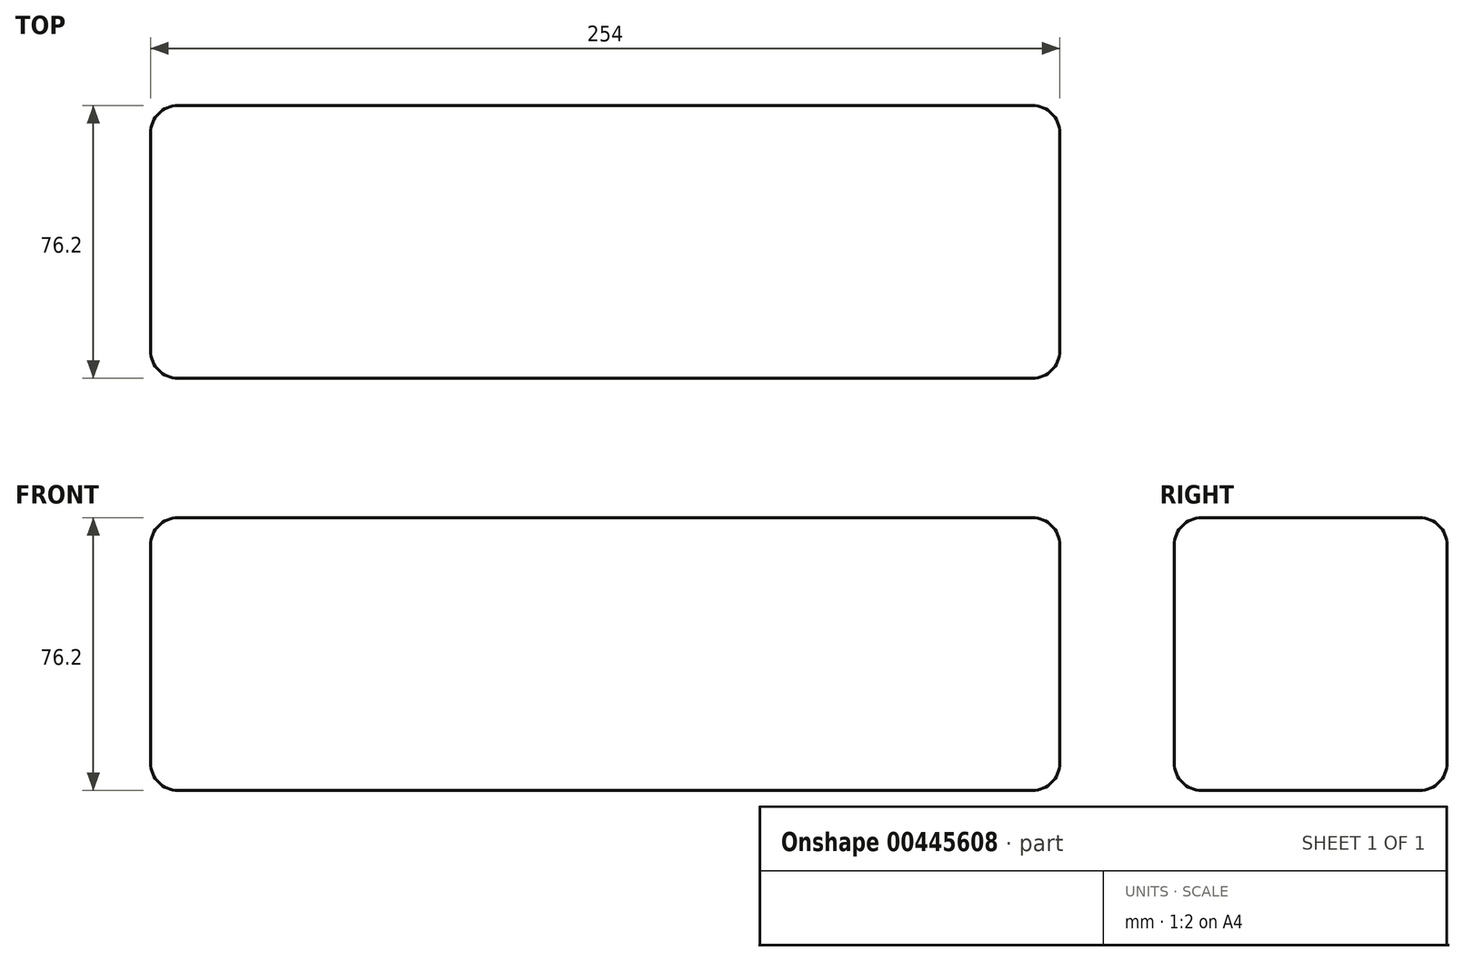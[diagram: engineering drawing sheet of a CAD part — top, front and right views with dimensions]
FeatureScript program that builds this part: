
annotation { "Feature Type Name" : "Feature", "Feature Type Description" : "" }
export const myFeature = defineFeature(function(context is Context, id is Id, definition is map)
    precondition{}
    {
        {
            var Q0;
            Q0=qCreatedBy(makeId("Top.planeOp"),FACE);
            var sketch = newSketch(context, id + "F0", { "sketchPlane" : qUnion([Q0])});
            skLineSegment(sketch, "E0.bottom", {"start": v(-127, -38.1) * mm, "end": v(127, -38.1) * mm});
            skLineSegment(sketch, "E0.top", {"start": v(-127, 38.1) * mm, "end": v(127, 38.1) * mm});
            skLineSegment(sketch, "E0.left", {"start": v(-127, -38.1) * mm, "end": v(-127, 38.1) * mm});
            skLineSegment(sketch, "E0.right", {"start": v(127, -38.1) * mm, "end": v(127, 38.1) * mm});
            skPoint(sketch, "E0.middle", {"position": v(0, 0) * mm});
            skSolve(sketch);
        }
        {
            var Q0;
            Q0 = qSketchRegion(id + "F0", true);
            extrude(context, id + "F1", {"entities" : qUnion([Q0]), "depth" : 50.8 * mm});
        }
        {
            var Q0;
            Q0=makeQuery(id+"F1.opExtrude","CAP_FACE",FACE,{"disambiguationData":[OSD([sQuery(id+"F0.wireOp",EDGE,"E0.bottom"),sQuery(id+"F0.wireOp",EDGE,"E0.top"),sQuery(id+"F0.wireOp",EDGE,"E0.left"),sQuery(id+"F0.wireOp",EDGE,"E0.right")])],"isStart":false});
            extrude(context, id + "F2", {"entities" : qUnion([Q0]), "operationType" : NewBodyOperationType.ADD, "depth" : 25.4 * mm});
        }
        {
            var Q0;
            Q0=makeQuery(id+"F2.opExtrude","CAP_EDGE",EDGE,{"disambiguationData":[OSD([sQuery(id+"F0.wireOp",EDGE,"E0.right")])],"isStart":false});
            var Q1;
            Q1=makeQuery(id+"F2.opExtrude","CAP_EDGE",EDGE,{"disambiguationData":[OSD([sQuery(id+"F0.wireOp",EDGE,"E0.top")])],"isStart":false});
            var Q2;
            Q2=makeQuery(id+"F2.opExtrude","CAP_EDGE",EDGE,{"disambiguationData":[OSD([sQuery(id+"F0.wireOp",EDGE,"E0.left")])],"isStart":false});
            var Q3;
            Q3=makeQuery(id+"F2.opExtrude","CAP_EDGE",EDGE,{"disambiguationData":[OSD([sQuery(id+"F0.wireOp",EDGE,"E0.bottom")])],"isStart":false});
            var Q4;
            {var subQ0=sQuery(id+"F0.wireOp",EDGE,"E0.right");var subQ1=sQuery(id+"F0.wireOp",EDGE,"E0.bottom");Q4=makeQuery(id+"F2.boolean.opBoolean","MERGE",EDGE,{"derivedFrom":[makeQuery(id+"F1.opExtrude","SWEPT_EDGE",EDGE,{"disambiguationData":[OSD([subQ1,subQ0])]}),makeQuery(id+"F2.opExtrude","SWEPT_EDGE",EDGE,{"disambiguationData":[OSD([subQ1,subQ0])]})]});}
            var Q5;
            {var subQ0=sQuery(id+"F0.wireOp",EDGE,"E0.right");var subQ1=sQuery(id+"F0.wireOp",EDGE,"E0.top");Q5=makeQuery(id+"F2.boolean.opBoolean","MERGE",EDGE,{"derivedFrom":[makeQuery(id+"F1.opExtrude","SWEPT_EDGE",EDGE,{"disambiguationData":[OSD([subQ1,subQ0])]}),makeQuery(id+"F2.opExtrude","SWEPT_EDGE",EDGE,{"disambiguationData":[OSD([subQ1,subQ0])]})]});}
            var Q6;
            Q6=makeQuery(id+"F1.opExtrude","CAP_EDGE",EDGE,{"disambiguationData":[OSD([sQuery(id+"F0.wireOp",EDGE,"E0.bottom")])],"isStart":true});
            var Q7;
            {var subQ0=sQuery(id+"F0.wireOp",EDGE,"E0.left");var subQ1=sQuery(id+"F0.wireOp",EDGE,"E0.bottom");Q7=makeQuery(id+"F2.boolean.opBoolean","MERGE",EDGE,{"derivedFrom":[makeQuery(id+"F1.opExtrude","SWEPT_EDGE",EDGE,{"disambiguationData":[OSD([subQ1,subQ0])]}),makeQuery(id+"F2.opExtrude","SWEPT_EDGE",EDGE,{"disambiguationData":[OSD([subQ1,subQ0])]})]});}
            var Q8;
            {var subQ0=sQuery(id+"F0.wireOp",EDGE,"E0.left");var subQ1=sQuery(id+"F0.wireOp",EDGE,"E0.top");Q8=makeQuery(id+"F2.boolean.opBoolean","MERGE",EDGE,{"derivedFrom":[makeQuery(id+"F1.opExtrude","SWEPT_EDGE",EDGE,{"disambiguationData":[OSD([subQ1,subQ0])]}),makeQuery(id+"F2.opExtrude","SWEPT_EDGE",EDGE,{"disambiguationData":[OSD([subQ1,subQ0])]})]});}
            var Q9;
            Q9=makeQuery(id+"F1.opExtrude","CAP_EDGE",EDGE,{"disambiguationData":[OSD([sQuery(id+"F0.wireOp",EDGE,"E0.left")])],"isStart":true});
            var Q10;
            Q10=makeQuery(id+"F1.opExtrude","CAP_FACE",FACE,{"disambiguationData":[OSD([sQuery(id+"F0.wireOp",EDGE,"E0.bottom"),sQuery(id+"F0.wireOp",EDGE,"E0.top"),sQuery(id+"F0.wireOp",EDGE,"E0.left"),sQuery(id+"F0.wireOp",EDGE,"E0.right")])],"isStart":true});
            fillet(context, id + "F3", {"entities" : qUnion([Q0, Q1, Q2, Q3, Q4, Q5, Q6, Q7, Q8, Q9, Q10]), "radius" : 7.62 * mm, "tangentPropagation" : true, "allowEdgeOverflow" : false});
        }
    });
